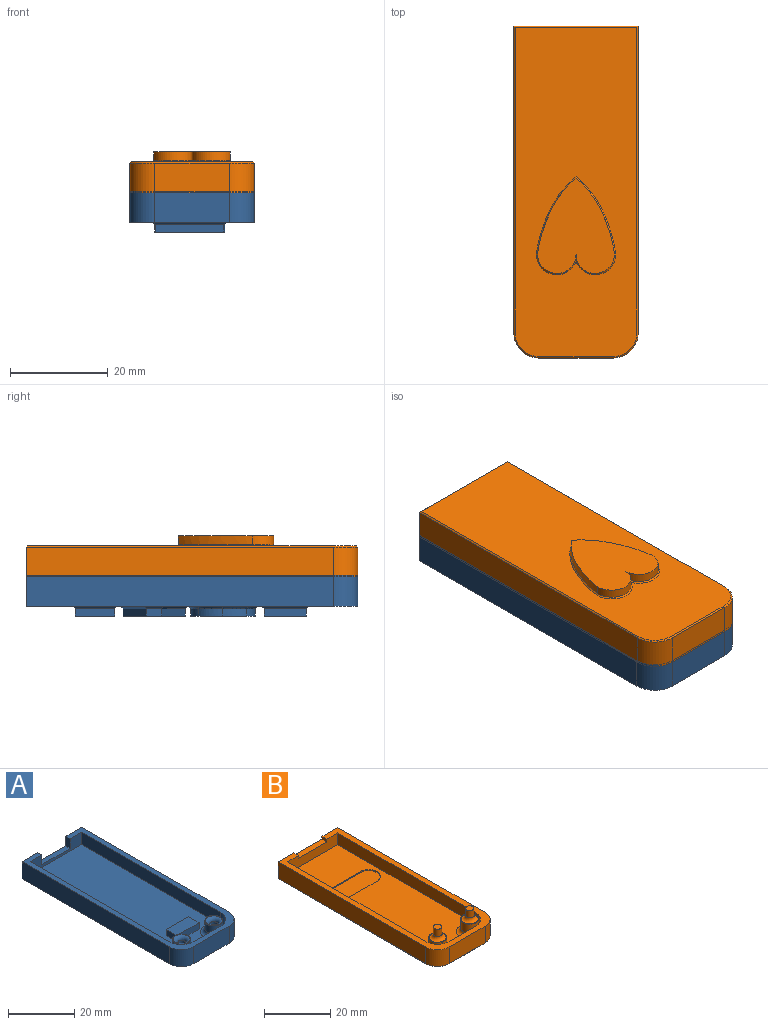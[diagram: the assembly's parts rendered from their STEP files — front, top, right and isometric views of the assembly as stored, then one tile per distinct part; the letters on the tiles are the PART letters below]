
ASSEMBLY  parts=2 mates=1
PART A: 123 faces, bbox 25.9x68.3x8.9 mm
  f0: plane 68.33x25.92mm, normal (0,0,-1), area 1236.3mm2, adj f2,f3,f4,f5,f21,f22,f82,f83
  f1: plane 67.82x25.4mm, normal (0,0,1), area 297.5mm2, adj f2,f3,f4,f5,f6,f7,f8,f9
  f2: plane 25.4x6.35mm, normal (0,1,0), area 118.7mm2, adj f0,f1,f4,f5,f11,f12,f13
  f3: plane 15.24x6.35mm, normal (0,-1,0), area 96.8mm2, adj f0,f1,f21,f22
  f4: plane 62.74x6.35mm, normal (1,0,0), area 398.4mm2, adj f0,f1,f2,f21
  f5: plane 62.74x6.35mm, normal (-1,0,0), area 398.4mm2, adj f0,f1,f2,f22
  f6: plane 11.68x4.57mm, normal (0,1,0), area 53.4mm2, adj f1,f10,f19,f20
  f7: plane 59.18x4.57mm, normal (-1,0,0), area 270.6mm2, adj f1,f8,f10,f20
  f8: plane 21.84x4.57mm, normal (0,-1,0), area 57.3mm2, adj f1,f7,f9,f10,f11,f12,f13
  f9: plane 59.18x4.57mm, normal (1,0,0), area 270.6mm2, adj f1,f8,f10,f19
  f10: plane 64.26x21.84mm, normal (0,0,1), area 1252.3mm2, adj f6,f7,f8,f9,f14,f15,f16,f17
  f11: plane 3.56x1.78mm, normal (-1,0,0), area 6.3mm2, adj f1,f2,f8,f12
  f12: plane 11.98x1.78mm, normal (0,0,1), area 21.3mm2, adj f2,f8,f11,f13
  f13: plane 3.56x1.78mm, normal (1,0,0), area 6.3mm2, adj f1,f2,f8,f12
  f14: plane 9.47x2.29mm, normal (0,-1,0), area 21.7mm2, adj f10,f15,f17,f18
  f15: plane 4.59x2.29mm, normal (1,0,0), area 10.5mm2, adj f10,f14,f16,f18
  f16: plane 9.47x2.29mm, normal (0,1,0), area 21.7mm2, adj f10,f15,f17,f18
  f17: plane 4.59x2.29mm, normal (-1,0,0), area 10.5mm2, adj f10,f14,f16,f18
  f18: plane 9.47x4.59mm, normal (0,0,1), area 43.5mm2, adj f14,f15,f16,f17
  f19: cylinder r=5.08mm len=5.08mm, axis (0,0,1), area 36.5mm2, adj f1,f6,f9,f10,f33
  f20: cylinder r=5.08mm len=5.08mm, axis (0,0,-1), area 36.5mm2, adj f1,f6,f7,f10,f31
  f21: cylinder r=5.08mm len=6.35mm, axis (0,0,1), area 50.7mm2, adj f0,f1,f3,f4
  f22: cylinder r=5.08mm len=6.35mm, axis (0,0,-1), area 50.7mm2, adj f0,f1,f3,f5
  f23: cylinder r=1.28mm len=2.79mm, axis (0,0,-1), area 22.4mm2, adj f26,f34
  f24: cylinder r=2.74mm len=5.47mm, axis (0,0,-1), area 48mm2, adj f25,f33
  f25: plane 5.47x5.47mm, normal (0,0,1), area 3.2mm2, adj f24,f34
  f26: plane 2.55x2.55mm, normal (0,0,1), area 5.1mm2, adj f23
  f27: cylinder r=2.74mm len=5.47mm, axis (0,0,-1), area 48mm2, adj f29,f31
  f28: cylinder r=1.28mm len=2.79mm, axis (0,0,-1), area 22.4mm2, adj f30,f32
  f29: plane 5.47x5.47mm, normal (0,0,1), area 3.2mm2, adj f27,f32
  f30: plane 2.55x2.55mm, normal (0,0,1), area 5.1mm2, adj f28
  f31: torus R=4.01mm, axis (0,0,1), area 38.1mm2, adj f10,f20,f27
  f32: torus R=2.55mm, axis (0,0,1), area 21.8mm2, adj f28,f29
  f33: torus R=4.01mm, axis (0,0,1), area 38.1mm2, adj f10,f19,f24
  f34: torus R=2.55mm, axis (0,0,1), area 21.8mm2, adj f23,f25
  f35: plane 13.9x1.52mm, normal (0,-1,0), area 21.2mm2, adj f36,f40,f41,f120
  f36: plane 8.58x1.52mm, normal (-1,0,0), area 13.1mm2, adj f35,f37,f41,f118
  f37: plane 2.43x1.52mm, normal (0,1,0), area 3.7mm2, adj f36,f38,f41,f117
  f38: plane 5.64x1.52mm, normal (1,0,0), area 8.6mm2, adj f37,f39,f41,f119
  f39: plane 11.47x1.52mm, normal (0,1,0), area 17.5mm2, adj f38,f40,f41,f121
  f40: plane 2.95x1.52mm, normal (1,0,0), area 4.5mm2, adj f35,f39,f41,f122
  f41: plane 13.9x8.58mm, normal (0,0,-1), area 54.7mm2, adj f35,f36,f37,f38,f39,f40
  f42: extruded ~3.51x1.52mm, area 5.6mm2, adj f43,f55,f56,f115
  f43: extruded ~3.51x1.52mm, area 5.6mm2, adj f42,f44,f56,f116
  f44: extruded ~2.65x1.52mm, area 4.6mm2, adj f43,f45,f56,f114
  f45: extruded ~4.69x3.51mm, area 10.2mm2, adj f44,f46,f56,f112
  f46: extruded ~4.69x3.53mm, area 10.2mm2, adj f45,f55,f56,f111
  f47: extruded ~5.31x1.71mm, area 8.7mm2, adj f48,f54,f56,f97
  f48: extruded ~5.3x1.7mm, area 8.7mm2, adj f47,f49,f56,f98
  f49: extruded ~4.9x1.85mm, area 8.2mm2, adj f48,f50,f56,f96
  f50: extruded ~4.92x1.83mm, area 8.2mm2, adj f49,f51,f56,f94
  f51: extruded ~5.3x1.72mm, area 8.7mm2, adj f50,f52,f56,f92
  f52: extruded ~5.33x1.71mm, area 8.7mm2, adj f51,f53,f56,f91
  f53: extruded ~4.91x1.85mm, area 8.2mm2, adj f52,f54,f56,f93
  f54: extruded ~4.91x1.85mm, area 8.2mm2, adj f47,f53,f56,f95
  f55: extruded ~2.64x1.52mm, area 4.6mm2, adj f42,f46,f56,f113
  f56: plane 14.31x13.23mm, normal (0,0,-1), area 101.2mm2, adj f42,f43,f44,f45,f46,f47,f48,f49
  f57: plane 8.8x6.47mm, normal (0,0,-1), area 42.3mm2, adj f111,f112,f113,f114,f115,f116
  f58: plane 2.98x1.52mm, normal (1,0,0), area 4.5mm2, adj f59,f67,f68,f85
  f59: plane 8.27x2.63mm, normal (0.3,-0.95,0), area 13.2mm2, adj f58,f60,f68,f87
  f60: extruded ~3.06x1.52mm, area 4.8mm2, adj f59,f61,f68,f89,f90
  f61: extruded ~1.52x1.35mm, area 2.1mm2, adj f60,f62,f68,f90
  f62: extruded ~1.71x1.52mm, area 2.7mm2, adj f61,f63,f68,f90
  f63: plane 8.27x2.62mm, normal (0.3,0.95,0), area 13.2mm2, adj f62,f64,f68,f88
  f64: plane 2.98x1.52mm, normal (1,0,0), area 4.5mm2, adj f63,f65,f68,f86
  f65: plane 13.9x4.72mm, normal (-0.32,-0.95,0), area 22.4mm2, adj f64,f66,f68,f84
  f66: plane 3.21x1.52mm, normal (-1,0,0), area 4.9mm2, adj f65,f67,f68,f82
  f67: plane 13.9x4.72mm, normal (-0.32,0.95,0), area 22.4mm2, adj f58,f66,f68,f83
  f68: plane 13.9x12.65mm, normal (0,0,-1), area 74.5mm2, adj f58,f59,f60,f61,f62,f63,f64,f65
  f69: plane 8x1.52mm, normal (-1,0,0), area 12.2mm2, adj f70,f80,f81,f110
  f70: plane 2.43x1.52mm, normal (0,1,0), area 3.7mm2, adj f69,f71,f81,f108
  f71: plane 5.06x1.52mm, normal (1,0,0), area 7.7mm2, adj f70,f72,f81,f106
  f72: plane 3.58x1.52mm, normal (0,1,0), area 5.5mm2, adj f71,f73,f81,f104
  f73: plane 4.71x1.52mm, normal (-1,0,0), area 7.2mm2, adj f72,f74,f81,f102
  f74: plane 2.42x1.52mm, normal (0,1,0), area 3.7mm2, adj f73,f75,f81,f100
  f75: plane 4.71x1.52mm, normal (1,0,0), area 7.2mm2, adj f74,f76,f81,f99
  f76: plane 3.05x1.52mm, normal (0,1,0), area 4.6mm2, adj f75,f77,f81,f101
  f77: plane 5.06x1.52mm, normal (-1,0,0), area 7.7mm2, adj f76,f78,f81,f103
  f78: plane 2.42x1.52mm, normal (0,1,0), area 3.7mm2, adj f77,f79,f81,f105
  f79: plane 8x1.52mm, normal (1,0,0), area 12.2mm2, adj f78,f80,f81,f107
  f80: plane 13.9x1.52mm, normal (0,-1,0), area 21.2mm2, adj f69,f79,f81,f109
  f81: plane 13.9x8mm, normal (0,0,-1), area 76.8mm2, adj f69,f70,f71,f72,f73,f74,f75,f76
  f82: plane 3.94x0.51mm, normal (-0.71,0,-0.71), area 2.6mm2, adj f0,f66,f83,f84
  f83: plane 14.91x5.43mm, normal (-0.23,0.67,-0.71), area 10.9mm2, adj f0,f67,f82,f85
  f84: plane 14.91x5.42mm, normal (-0.23,-0.67,-0.71), area 10.9mm2, adj f0,f65,f82,f86
  f85: plane 4.06x0.51mm, normal (0.71,0,-0.71), area 2.5mm2, adj f0,f58,f83,f87
  f86: plane 4.06x0.51mm, normal (0.71,0,-0.71), area 2.5mm2, adj f0,f64,f84,f88
  f87: plane 8.78x3.12mm, normal (0.21,-0.67,-0.71), area 6.4mm2, adj f0,f59,f85,f89
  f88: plane 8.79x3.1mm, normal (0.21,0.67,-0.71), area 6.4mm2, adj f0,f63,f86,f90
  f89: bspline ~3.52x1.29mm, area 1.4mm2, adj f0,f60,f87,f90
  f90: bspline ~3.31x1.33mm, area 1.4mm2, adj f0,f60,f61,f62,f88,f89
  f91: bspline ~5.67x2.22mm, area 4.3mm2, adj f0,f52,f92,f93
  f92: bspline ~5.65x2.22mm, area 4.2mm2, adj f0,f51,f91,f94
  f93: bspline ~5.28x2.36mm, area 4mm2, adj f0,f53,f91,f95
  f94: bspline ~5.29x2.34mm, area 4mm2, adj f0,f50,f92,f96
  f95: bspline ~5.28x2.36mm, area 4mm2, adj f0,f54,f93,f97
  f96: bspline ~5.27x2.35mm, area 4mm2, adj f0,f49,f94,f98
  f97: bspline ~5.65x2.22mm, area 4.2mm2, adj f0,f47,f95,f98
  f98: bspline ~5.65x2.21mm, area 4.2mm2, adj f0,f48,f96,f97
  f99: plane 5.21x0.51mm, normal (0.71,0,-0.71), area 3.4mm2, adj f0,f75,f100,f101
  f100: plane 3.43x0.51mm, normal (0,0.71,-0.71), area 2.1mm2, adj f0,f74,f99,f102
  f101: plane 3.05x0.51mm, normal (0,0.71,-0.71), area 1.8mm2, adj f0,f76,f99,f103
  f102: plane 5.21x0.51mm, normal (-0.71,0,-0.71), area 3.4mm2, adj f0,f73,f100,f104
  f103: plane 5.56x0.51mm, normal (-0.71,0,-0.71), area 3.6mm2, adj f0,f77,f101,f105
  f104: plane 3.58x0.51mm, normal (0,0.71,-0.71), area 2.2mm2, adj f0,f72,f102,f106
  f105: plane 3.43x0.51mm, normal (0,0.71,-0.71), area 2.1mm2, adj f0,f78,f103,f107
  f106: plane 5.56x0.51mm, normal (0.71,0,-0.71), area 3.6mm2, adj f0,f71,f104,f108
  f107: plane 9.02x0.51mm, normal (0.71,0,-0.71), area 6.1mm2, adj f0,f79,f105,f109
  f108: plane 3.45x0.51mm, normal (0,0.71,-0.71), area 2.1mm2, adj f0,f70,f106,f110
  f109: plane 14.91x0.51mm, normal (0,-0.71,-0.71), area 10.3mm2, adj f0,f80,f107,f110
  f110: plane 9.02x0.51mm, normal (-0.71,0,-0.71), area 6.1mm2, adj f0,f69,f108,f109
  f111: bspline ~4.69x3.53mm, area 4.5mm2, adj f46,f57,f112,f113
  f112: bspline ~4.69x3.51mm, area 4.5mm2, adj f45,f57,f111,f114
  f113: bspline ~2.64x1.48mm, area 2mm2, adj f55,f57,f111,f115
  f114: bspline ~2.65x1.49mm, area 2mm2, adj f44,f57,f112,f116
  f115: bspline ~3.51x1.29mm, area 2.5mm2, adj f42,f57,f113,f116
  f116: bspline ~3.51x1.3mm, area 2.5mm2, adj f43,f57,f114,f115
  f117: plane 3.45x0.51mm, normal (0,0.71,-0.71), area 2.1mm2, adj f0,f37,f118,f119
  f118: plane 9.6x0.51mm, normal (-0.71,0,-0.71), area 6.5mm2, adj f0,f36,f117,f120
  f119: plane 6.14x0.51mm, normal (0.71,0,-0.71), area 4mm2, adj f0,f38,f117,f121
  f120: plane 14.91x0.51mm, normal (0,-0.71,-0.71), area 10.3mm2, adj f0,f35,f118,f122
  f121: plane 11.97x0.51mm, normal (0,0.71,-0.71), area 8.2mm2, adj f0,f39,f119,f122
  f122: plane 3.96x0.51mm, normal (0.71,0,-0.71), area 2.5mm2, adj f0,f40,f120,f121
PART B: 50 faces, bbox 25.6x68.1x12.8 mm
  f0: plane 67.55x25.13mm, normal (0,0,-1), area 1442.3mm2, adj f36,f37,f38,f39,f40,f41,f42,f43
  f1: plane 63.75x21.34mm, normal (0,0,1), area 1138mm2, adj f7,f8,f9,f10,f14,f15,f26,f27
  f2: plane 67.82x25.4mm, normal (0,0,1), area 338mm2, adj f3,f4,f5,f6,f7,f8,f9,f10
  f3: plane 25.4x6.1mm, normal (0,1,0), area 142.7mm2, adj f2,f5,f6,f11,f12,f13,f44
  f4: plane 15.24x6.1mm, normal (0,-1,0), area 92.9mm2, adj f2,f16,f17,f41
  f5: plane 62.74x6.1mm, normal (1,0,0), area 382.5mm2, adj f2,f3,f16,f42
  f6: plane 62.74x6.1mm, normal (-1,0,0), area 382.5mm2, adj f2,f3,f17,f45
  f7: plane 11.18x4.32mm, normal (0,1,0), area 48.3mm2, adj f1,f2,f14,f15,f46,f47
  f8: plane 58.67x4.32mm, normal (-1,0,0), area 253.4mm2, adj f1,f2,f9,f15
  f9: plane 21.34x4.32mm, normal (0,-1,0), area 79.9mm2, adj f1,f2,f8,f10,f11,f12,f13
  f10: plane 58.67x4.32mm, normal (1,0,0), area 253.4mm2, adj f1,f2,f9,f14
  f11: plane 2.03x1.02mm, normal (-1,0,0), area 2.1mm2, adj f2,f3,f9,f12
  f12: plane 11.99x2.03mm, normal (0,0,1), area 24.4mm2, adj f3,f9,f11,f13
  f13: plane 2.03x1.02mm, normal (1,0,0), area 2.1mm2, adj f2,f3,f9,f12
  f14: cylinder r=5.08mm len=5.08mm, axis (0,0,1), area 33.4mm2, adj f1,f2,f7,f10,f47
  f15: cylinder r=5.08mm len=5.08mm, axis (0,0,-1), area 33.4mm2, adj f1,f2,f7,f8,f46
  f16: cylinder r=5.08mm len=6.1mm, axis (0,0,1), area 48.6mm2, adj f2,f4,f5,f40
  f17: cylinder r=5.08mm len=6.1mm, axis (0,0,-1), area 48.6mm2, adj f2,f4,f6,f43
  f18: cylinder r=2.73mm len=5.46mm, axis (0,0,-1), area 56.6mm2, adj f19,f47
  f19: plane 5.46x5.46mm, normal (0,0,1), area 3.2mm2, adj f18,f49
  f20: cylinder r=2.73mm len=5.46mm, axis (0,0,-1), area 56.6mm2, adj f21,f46
  f21: plane 5.46x5.46mm, normal (0,0,1), area 3.2mm2, adj f20,f48
  f22: cylinder r=1.27mm len=2.67mm, axis (0,0,-1), area 21.3mm2, adj f23,f49
  f23: plane 2.54x2.54mm, normal (0,0,1), area 5.1mm2, adj f22
  f24: cylinder r=1.27mm len=2.67mm, axis (0,0,-1), area 21.3mm2, adj f25,f48
  f25: plane 2.54x2.54mm, normal (0,0,1), area 5.1mm2, adj f24
  f26: plane 11.18x0.38mm, normal (0,-1,0), area 4.3mm2, adj f1,f27,f29,f30
  f27: cylinder r=3.56mm len=7.11mm, axis (0,0,1), area 4.3mm2, adj f1,f26,f28,f30
  f28: plane 11.18x0.38mm, normal (0,1,0), area 4.3mm2, adj f1,f27,f29,f30
  f29: cylinder r=3.56mm len=7.11mm, axis (0,0,1), area 4.3mm2, adj f1,f26,f28,f30
  f30: plane 18.29x7.11mm, normal (0,0,1), area 119.2mm2, adj f26,f27,f28,f29
  f31: extruded ~15.2x7.82mm, area 31.1mm2, adj f32,f34,f35,f36
  f32: extruded ~15.2x7.82mm, area 31.1mm2, adj f31,f33,f35,f38
  f33: cylinder r=3.92mm len=7.83mm, axis (0,0,1), area 22.5mm2, adj f32,f34,f35,f39
  f34: cylinder r=3.92mm len=7.83mm, axis (0,0,1), area 22.5mm2, adj f31,f33,f35,f37
  f35: plane 19.45x15.66mm, normal (0,0,-1), area 208.4mm2, adj f31,f32,f33,f34
  f36: bspline ~15.53x8.23mm, area 6.4mm2, adj f0,f31,f37,f38
  f37: cone r=3.92mm half-angle=45deg, axis (0,0,1), area 4.4mm2, adj f0,f34,f36,f39
  f38: bspline ~16.09x8.93mm, area 6.4mm2, adj f0,f32,f36,f39
  f39: cone r=4.17mm half-angle=45deg, axis (0,0,1), area 4.4mm2, adj f0,f33,f37,f38
  f40: cone r=4.83mm half-angle=45deg, axis (0,0,1), area 2.8mm2, adj f0,f16,f41,f42
  f41: plane 15.24x0.25mm, normal (0,-0.71,-0.71), area 5.5mm2, adj f0,f4,f40,f43
  f42: plane 62.74x0.25mm, normal (0.71,0,-0.71), area 22.5mm2, adj f0,f5,f40,f44
  f43: cone r=4.83mm half-angle=45deg, axis (0,0,1), area 2.8mm2, adj f0,f17,f41,f45
  f44: plane 25.4x0.25mm, normal (0,0.71,-0.71), area 9mm2, adj f0,f3,f42,f45
  f45: plane 62.74x0.25mm, normal (-0.71,0,-0.71), area 22.5mm2, adj f0,f6,f43,f44
  f46: torus R=4mm, axis (0,0,1), area 35.5mm2, adj f1,f7,f15,f20
  f47: torus R=4mm, axis (0,0,1), area 35.5mm2, adj f1,f7,f14,f18
  f48: torus R=2.54mm, axis (0,0,1), area 21.7mm2, adj f21,f24
  f49: torus R=2.54mm, axis (0,0,1), area 21.7mm2, adj f19,f22
PLACE A t=(-3.82,-2.53,-12.26)mm
PLACE B rot(axis=(0,1,0),180deg) t=(-3.81,-2.54,0.06)mm
MATE fastened B.f18 <-> A.f27  axis (0,0,-1) through (3.02,-30.71,-10.48)mm
